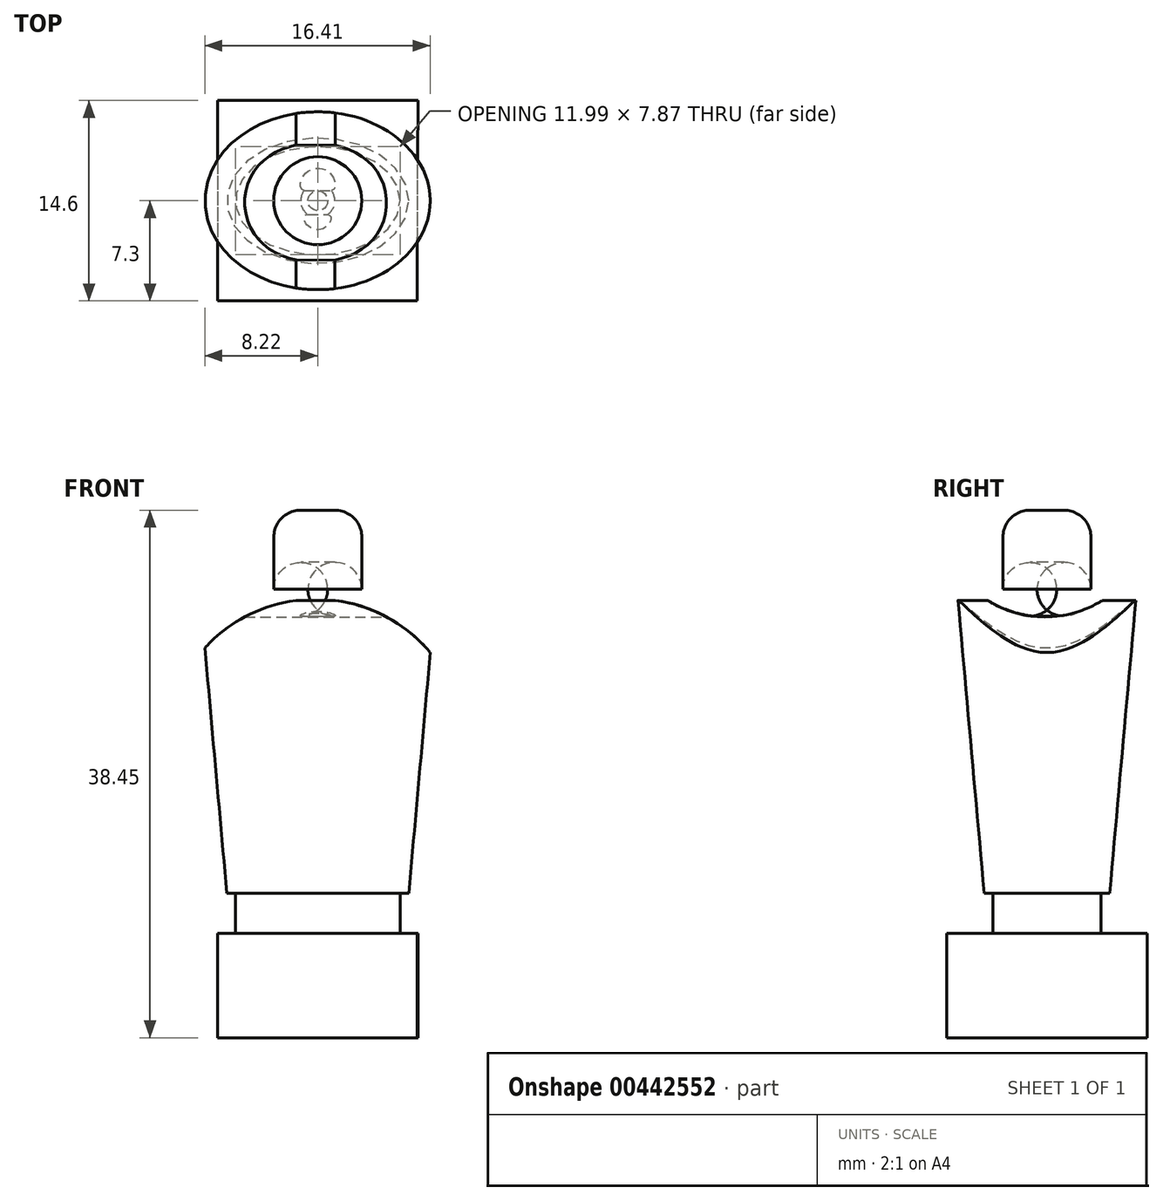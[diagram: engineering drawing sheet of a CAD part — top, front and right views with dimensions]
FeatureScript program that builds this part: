
annotation { "Feature Type Name" : "Feature", "Feature Type Description" : "" }
export const myFeature = defineFeature(function(context is Context, id is Id, definition is map)
    precondition{}
    {
        {
            var Q0;
            Q0=qCreatedBy(makeId("Top.planeOp"),FACE);
            var sketch = newSketch(context, id + "F0", { "sketchPlane" : qUnion([Q0])});
            skLineSegment(sketch, "E0", {"start": v(0, 7.3) * mm, "end": v(0, -7.3) * mm, "construction": true});
            skLineSegment(sketch, "E1", {"start": v(-7.3, 0) * mm, "end": v(7.3, 0) * mm, "construction": true});
            skLineSegment(sketch, "E2", {"start": v(-7.3, 7.3) * mm, "end": v(-7.3, -7.28) * mm});
            skLineSegment(sketch, "E3", {"start": v(-7.3, -7.28) * mm, "end": v(7.24, -7.3) * mm});
            skLineSegment(sketch, "E4", {"start": v(7.24, -7.3) * mm, "end": v(7.3, 7.3) * mm});
            skLineSegment(sketch, "E5", {"start": v(7.3, 7.3) * mm, "end": v(-7.3, 7.3) * mm});
            skSolve(sketch);
        }
        {
            var Q0;
            Q0 = qSketchRegion(id + "F0", true);
            extrude(context, id + "F1", {"entities" : qUnion([Q0]), "depth" : 7.62 * mm});
        }
        {
            var Q0;
            Q0=qCreatedBy(makeId("Top.planeOp"),FACE);
            cPlane(context, id + "F2", {"entities" : qUnion([Q0]), "cplaneType" : CPlaneType.OFFSET, "offset" : 7.62 * mm, "width" : 152.4 * mm, "height" : 152.4 * mm});
        }
        {
            var Q0;
            Q0=qCreatedBy(id+"F2.planeOp",FACE);
            var sketch = newSketch(context, id + "F3", { "sketchPlane" : qUnion([Q0])});
            skEllipse(sketch, "E6", {"center": v(0, 0) * mm, "majorRadius": 6 * mm, "minorRadius": 3.94 * mm, "majorAxis": v(1, 0)});
            skSolve(sketch);
        }
        {
            var Q0;
            Q0 = qSketchRegion(id + "F3", true);
            extrude(context, id + "F4", {"entities" : qUnion([Q0]), "operationType" : NewBodyOperationType.ADD, "depth" : 2.92 * mm});
        }
        {
            var Q0;
            Q0=makeQuery(id+"F4.opExtrude","CAP_FACE",FACE,{"disambiguationData":[OSD([sQuery(id+"F3.wireOp",EDGE,"E6")])],"isStart":false});
            cPlane(context, id + "F5", {"entities" : qUnion([Q0]), "cplaneType" : CPlaneType.OFFSET, "offset" : 0 * mm, "width" : 152.4 * mm, "height" : 152.4 * mm});
        }
        {
            var Q0;
            Q0=qCreatedBy(id+"F5.planeOp",FACE);
            var sketch = newSketch(context, id + "F6", { "sketchPlane" : qUnion([Q0])});
            skEllipse(sketch, "E7", {"center": v(0, 0) * mm, "majorRadius": 6.63 * mm, "minorRadius": 4.57 * mm, "majorAxis": v(1, 0)});
            skSolve(sketch);
        }
        {
            var Q0;
            Q0=qCreatedBy(id+"F5.planeOp",FACE);
            cPlane(context, id + "F7", {"entities" : qUnion([Q0]), "cplaneType" : CPlaneType.OFFSET, "offset" : 21.34 * mm, "width" : 152.4 * mm, "height" : 152.4 * mm});
        }
        {
            var Q0;
            Q0=qCreatedBy(id+"F7.planeOp",FACE);
            var sketch = newSketch(context, id + "F8", { "sketchPlane" : qUnion([Q0])});
            skEllipse(sketch, "E8", {"center": v(0, 0) * mm, "majorRadius": 8.53 * mm, "minorRadius": 6.48 * mm, "majorAxis": v(1, 0)});
            skSolve(sketch);
        }
        {
            var Q1;
            Q1=makeQuery(id+"F6.imprint","IMPRINT",FACE,{"disambiguationData":[TD([[makeQuery(id+"F6.imprint","IMPRINT",EDGE,{"derivedFrom":sQuery(id+"F6.wireOp",EDGE,"E7")}),1.0]])]});
            var Q2;
            Q2=makeQuery(id+"F8.imprint","IMPRINT",FACE,{"disambiguationData":[TD([[makeQuery(id+"F8.imprint","IMPRINT",EDGE,{"derivedFrom":sQuery(id+"F8.wireOp",EDGE,"E8")}),1.0]])]});
            loft(context, id + "F9", {"operationType" : NewBodyOperationType.ADD, "sheetProfilesArray" : [{ "sheetProfileEntities" : qUnion([Q1]) }, { "sheetProfileEntities" : qUnion([Q2]) }]});
        }
        {
            var Q0;
            Q0=makeQuery(id+"F1.opExtrude","SWEPT_FACE",FACE,{"disambiguationData":[OSD([sQuery(id+"F0.wireOp",EDGE,"E3")])]});
            var sketch = newSketch(context, id + "F10", { "sketchPlane" : qUnion([Q0])});
            skArc(sketch, "E9", {"start": v(8.27, 27.99) * mm, "mid": v(0.08, 31.97) * mm, "end": v(-8.28, 28.35) * mm});
            skLineSegment(sketch, "E10", {"start": v(-8.28, 28.35) * mm, "end": v(-8.58, 32.2) * mm});
            skLineSegment(sketch, "E11", {"start": v(-8.58, 32.2) * mm, "end": v(8.58, 32.2) * mm});
            skLineSegment(sketch, "E12", {"start": v(8.27, 27.99) * mm, "end": v(8.58, 32.2) * mm});
            skSolve(sketch);
        }
        {
            var Q0;
            Q0 = qSketchRegion(id + "F10", true);
            extrude(context, id + "F11", {"entities" : qUnion([Q0]), "operationType" : NewBodyOperationType.REMOVE, "oppositeDirection" : true, "depth" : 25.4 * mm});
        }
        {
            var Q0;
            Q0=makeQuery(id+"F1.opExtrude","SWEPT_FACE",FACE,{"disambiguationData":[OSD([sQuery(id+"F0.wireOp",EDGE,"E4")])]});
            var sketch = newSketch(context, id + "F12", { "sketchPlane" : qUnion([Q0])});
            skLineSegment(sketch, "E13", {"start": v(-4.37, 31.9) * mm, "end": v(4.1, 31.9) * mm});
            skArc(sketch, "E14", {"start": v(-4.37, 31.9) * mm, "mid": v(-0.13, 30.67) * mm, "end": v(4.1, 31.9) * mm});
            skSolve(sketch);
        }
        {
            var Q0;
            Q0=makeQuery(id+"F12.imprint","IMPRINT",FACE,{"disambiguationData":[TD([[makeQuery(id+"F12.imprint","IMPRINT",EDGE,{"derivedFrom":sQuery(id+"F12.wireOp",EDGE,"E13")}),-1.0]])]});
            extrude(context, id + "F13", {"entities" : qUnion([Q0]), "operationType" : NewBodyOperationType.REMOVE, "oppositeDirection" : true, "depth" : 25.4 * mm});
        }
        {
            var Q0;
            Q0=qCreatedBy(makeId("Right.planeOp"),FACE);
            var sketch = newSketch(context, id + "F14", { "sketchPlane" : qUnion([Q0])});
            skLineSegment(sketch, "E15", {"start": v(3.2, 30.72) * mm, "end": v(0, 30.72) * mm});
            skLineSegment(sketch, "E16", {"start": v(3.2, 30.72) * mm, "end": v(3.2, 38.45) * mm});
            skLineSegment(sketch, "E17", {"start": v(3.2, 38.45) * mm, "end": v(0, 38.45) * mm});
            skLineSegment(sketch, "E18", {"start": v(0, 30.72) * mm, "end": v(0, 38.45) * mm});
            skSolve(sketch);
        }
        {
            var Q0;
            Q0=makeQuery(id+"F14.imprint","IMPRINT",FACE,{"disambiguationData":[TD([[makeQuery(id+"F14.imprint","IMPRINT",EDGE,{"derivedFrom":sQuery(id+"F14.wireOp",EDGE,"E15")}),-1.0]])]});
            var Q1;
            Q1=sQuery(id+"F14.wireOp",EDGE,"E18");
            revolve(context, id + "F15", {"operationType" : NewBodyOperationType.ADD, "entities" : qUnion([Q0]), "axis" : qUnion([Q1]), "revolveType" : RevolveType.FULL});
        }
        {
            var Q0;
            Q0=makeQuery(id+"F15.boolean.opBoolean","SPLIT",EDGE,{"disambiguationData":[OD(1.0)],"derivedFrom":makeQuery(id+"F15.opRevolve","SWEPT_EDGE",EDGE,{"disambiguationData":[OSD([sQuery(id+"F14.wireOp",EDGE,"E15"),sQuery(id+"F14.wireOp",EDGE,"E16")])]})});
            var Q1;
            Q1=makeQuery(id+"F15.opRevolve","SWEPT_EDGE",EDGE,{"disambiguationData":[OSD([sQuery(id+"F14.wireOp",EDGE,"E16"),sQuery(id+"F14.wireOp",EDGE,"E17")])]});
            fillet(context, id + "F16", {"entities" : qUnion([Q0, Q1]), "radius" : 1.96 * mm, "tangentPropagation" : true, "allowEdgeOverflow" : false});
        }
    });
